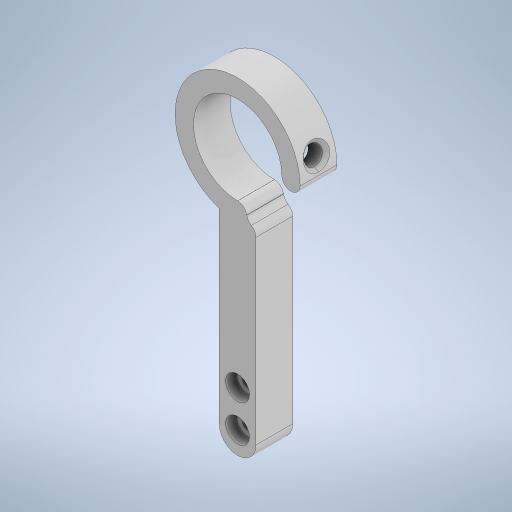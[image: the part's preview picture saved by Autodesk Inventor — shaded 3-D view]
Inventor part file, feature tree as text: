
AUTODESK INVENTOR PART (.ipt)
format: ipt  version: 2023.1 (Build 271208000, 208)  size: 325,632 bytes
history: native  units: mm
features: sketch x4, extrude x3, fillet x2, other x1, revolve x1, chamfer x1
ambient origin geometry x8: Origin, YZ Plane, XZ Plane, XY Plane, X Axis, Y Axis, Z Axis, Center Point
bodies: Body1 (feature_tree)
feature tree (12):
  other  "솔리드1"
  extrude  "돌출1"  Depth=10.0mm
  fillet  "모깎기1"  Radius=60.0mm
  revolve  "회전1"
  chamfer  "모따기1"  Distance=24.0mm
  extrude  "돌출2"  Depth=34.0mm
  fillet  "모깎기2"  Radius=10.0mm
  extrude  "돌출3"  Depth=2.5mm
  sketch  "스케치1"
  sketch  "스케치2"
  sketch  "스케치3"
  sketch  "스케치4"
